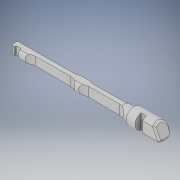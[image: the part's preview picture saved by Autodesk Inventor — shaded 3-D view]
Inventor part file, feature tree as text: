
AUTODESK INVENTOR PART (.ipt)
format: ipt  version: 2018.3 (Build 223284000, 284)  size: 246,784 bytes
history: native  units: in
note: dims shown in document units (in); Inventor stores cm internally (conversion verified against a paired STEP export)
features: sketch x3, extrude x3, revolve x1, chamfer x1
ambient origin geometry x8: Origin, YZ Plane, XZ Plane, XY Plane, X Axis, Y Axis, Z Axis, Center Point
bodies: Solid1 (feature_tree)
feature tree (8):
  sketch  "Sketch1"  dims[d0=0.27in d1=0.076in]
  revolve  "Revolution1"  [1 undecoded]
  extrude  "Extrusion1"  Depth=0.099in
  extrude  "Extrusion2"  Depth=0.125in
  extrude  "Extrusion3"  Depth=0.125in
  chamfer  "Chamfer1"  Distance=2.32in
  sketch  "Sketch2"  dims[d2=0.046in d3=0.099in]
  sketch  "Sketch3"  dims[d4=0.02in d5=0.01in d6=0.078in d7=2.32in d8=2.262in d9=0.16in d10=0.099in d11=0.14in d12=0.101in d13=0.03in d14=0.1035in d15=0.005in d16=0.01in d17=0.32in d18=0.32in d19=0.32in d20=0.32in d21=0.22in d22=0.56in d23=0.33in d24=1.53in d25=0.4in d27=90.0deg d28=1.0in d29=0.0in d30=0.28in d31=0.0in d32=0.142in d33=0.18in d34=0.28in d35=0.0in d36=0.03in d37=0.125in d38=45.0deg]
note: 1 required parameter value undecoded (feature->parameter linkage not recoverable at this tier; creation-order binding heuristic only, values carry confidence <= 0.55)
